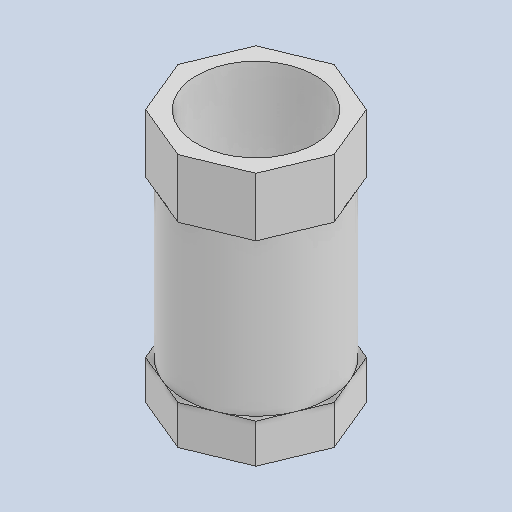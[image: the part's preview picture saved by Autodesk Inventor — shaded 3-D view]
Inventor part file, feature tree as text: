
AUTODESK INVENTOR PART (.ipt)
format: ipt  version: 2024 (Build 280153000, 153)  size: 147,968 bytes
history: native  units: mm
features: other x4, sketch x4
ambient origin geometry x8: Origin, YZ Plane, XZ Plane, XY Plane, X Axis, Y Axis, Z Axis, Center Point
bodies: Body1 (feature_tree)
feature tree (8):
  other  "TUBO_METALICO_B.ipt"
  other  "Sólido1::TUBO_METALICO_B.ipt"
  other  "OperaciónIdentificador1"
  sketch  "Boceto1"  dims[d0=10.0mm]
  sketch  "Boceto2"
  sketch  "Boceto3"
  sketch  "Boceto4"
  other  "Sólido1"
